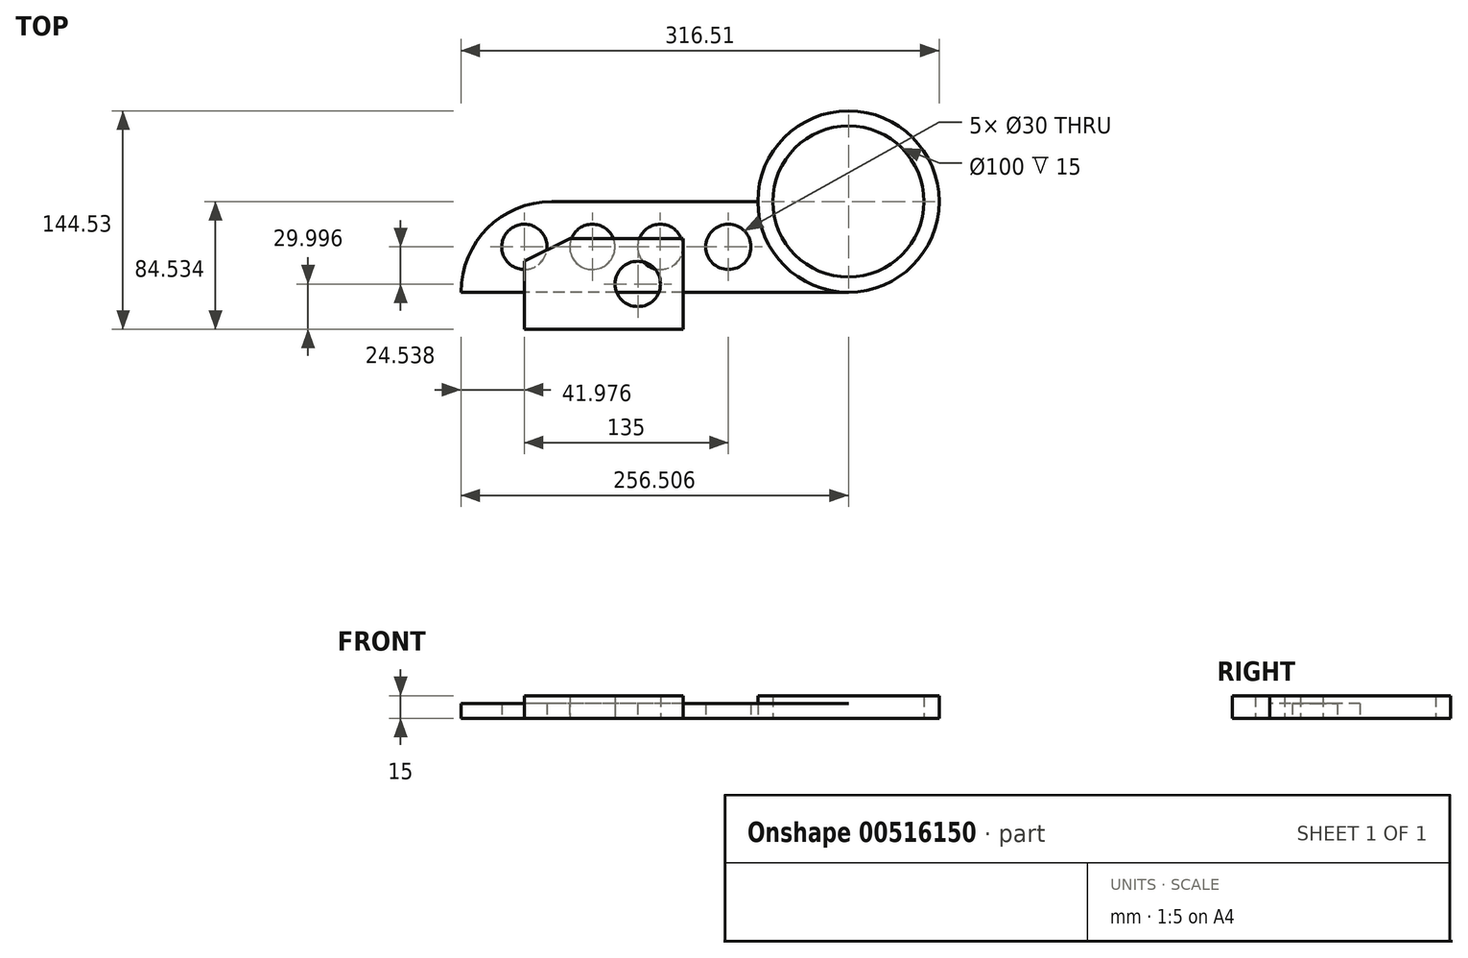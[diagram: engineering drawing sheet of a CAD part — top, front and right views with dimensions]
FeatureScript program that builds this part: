
annotation { "Feature Type Name" : "Feature", "Feature Type Description" : "" }
export const myFeature = defineFeature(function(context is Context, id is Id, definition is map)
    precondition{}
    {
        {
            assignVariable(context, id + "F0", {"name" : "hole_size", "anyValue" : 30});
        }
        {
            var Q0;
            Q0=qCreatedBy(makeId("Top.planeOp"),FACE);
            var sketch = newSketch(context, id + "F1", { "sketchPlane" : qUnion([Q0])});
            skLineSegment(sketch, "E0", {"start": v(97, 48.04) * mm, "end": v(-39.5, 48.04) * mm});
            skLineSegment(sketch, "E1", {"start": v(-39.5, 48.04) * mm, "end": v(-39.5, -11.96) * mm, "construction": true});
            skLineSegment(sketch, "E2", {"start": v(-39.5, -11.96) * mm, "end": v(157, -11.96) * mm});
            skArc(sketch, "E3", {"start": v(-39.5, 48.04) * mm, "mid": v(-81.93, 30.47) * mm, "end": v(-99.5, -11.96) * mm});
            skLineSegment(sketch, "E4", {"start": v(-39.5, -11.96) * mm, "end": v(-99.5, -11.96) * mm});
            skCircle(sketch, "E5", {"center": v(157, 48.04) * mm, "radius": 60 * mm});
            skLineSegment(sketch, "E6", {"start": v(97, 48.04) * mm, "end": v(157, 48.04) * mm, "construction": true});
            skCircle(sketch, "E7.0", {"center": v(157, 48.04) * mm, "radius": 50 * mm});
            skArc(sketch, "E8.0", {"start": v(-39.5, 38.04) * mm, "mid": v(-74.86, 23.4) * mm, "end": v(-89.5, -11.96) * mm, "construction": true});
            skCircle(sketch, "E9", {"center": v(-57.53, 18.04) * mm, "radius": 15 * mm});
            skLineSegment(sketch, "E10", {"start": v(-57.53, 18.04) * mm, "end": v(-57.53, -11.96) * mm, "construction": true});
            skLineSegment(sketch, "E11", {"start": v(77.47, -11.96) * mm, "end": v(77.47, 18.04) * mm, "construction": true});
            skCircle(sketch, "E12", {"center": v(77.47, 18.04) * mm, "radius": 15 * mm});
            skCircle(sketch, "E13.0", {"center": v(157, 48.04) * mm, "radius": 70 * mm, "construction": true});
            skCircle(sketch, "E14.1.0.0", {"center": v(-12.53, 18.04) * mm, "radius": 15 * mm});
            skCircle(sketch, "E14.2.0.0", {"center": v(32.47, 18.04) * mm, "radius": 15 * mm});
            skLineSegment(sketch, "E14.direction1", {"start": v(-57.53, 18.04) * mm, "end": v(-12.53, 18.04) * mm, "construction": true});
            skSolve(sketch);
        }
        {
            var Q0;
            Q0=makeQuery(id+"F1.imprint","IMPRINT",FACE,{"disambiguationData":[TD([[makeQuery(id+"F1.imprint","IMPRINT",EDGE,{"derivedFrom":sQuery(id+"F1.wireOp",EDGE,"E7.0")}),-1.0]])]});
            extrude(context, id + "F2", {"entities" : qUnion([Q0]), "depth" : (getVariable(context, 'hole_size') / 2) * mm, "offsetDistance" : 25 * mm});
        }
        {
            var Q0;
            {var subQ1=sQuery(id+"F1.wireOp",EDGE,"E0");Q0=makeQuery(id+"F1.imprint","IMPRINT",FACE,{"disambiguationData":[TD([[makeQuery(id+"F1.imprint","IMPRINT",EDGE,{"derivedFrom":subQ1}),1.0]])]});}
            extrude(context, id + "F3", {"entities" : qUnion([Q0]), "operationType" : NewBodyOperationType.ADD, "depth" : (getVariable(context, 'hole_size') / 3) * mm, "offsetDistance" : 25 * mm});
        }
        {
            var Q0;
            Q0=qCreatedBy(makeId("Top.planeOp"),FACE);
            var sketch = newSketch(context, id + "F4", { "sketchPlane" : qUnion([Q0])});
            skLineSegment(sketch, "E15", {"start": v(-27.42, 23.5) * mm, "end": v(47.58, 23.5) * mm});
            skLineSegment(sketch, "E16", {"start": v(47.58, 23.5) * mm, "end": v(47.58, -36.5) * mm});
            skLineSegment(sketch, "E17", {"start": v(47.58, -36.5) * mm, "end": v(-57.42, -36.5) * mm});
            skCircle(sketch, "E18", {"center": v(17.58, -6.5) * mm, "radius": 15 * mm});
            skLineSegment(sketch, "E19", {"start": v(-57.42, -36.5) * mm, "end": v(-57.42, 8.5) * mm});
            skLineSegment(sketch, "E20", {"start": v(-57.42, 8.5) * mm, "end": v(-27.42, 23.5) * mm});
            skLineSegment(sketch, "E21", {"start": v(-27.42, 23.5) * mm, "end": v(-27.42, 8.5) * mm, "construction": true});
            skLineSegment(sketch, "E22", {"start": v(-27.42, 8.5) * mm, "end": v(-57.42, 8.5) * mm, "construction": true});
            skSolve(sketch);
        }
        {
            var Q0;
            Q0=makeQuery(id+"F4.imprint","IMPRINT",FACE,{"disambiguationData":[TD([[makeQuery(id+"F4.imprint","IMPRINT",EDGE,{"derivedFrom":sQuery(id+"F4.wireOp",EDGE,"E15")}),-1.0]])]});
            extrude(context, id + "F5", {"entities" : qUnion([Q0]), "depth" : (getVariable(context, 'hole_size') / 2) * mm, "offsetDistance" : 25 * mm});
        }
    });
